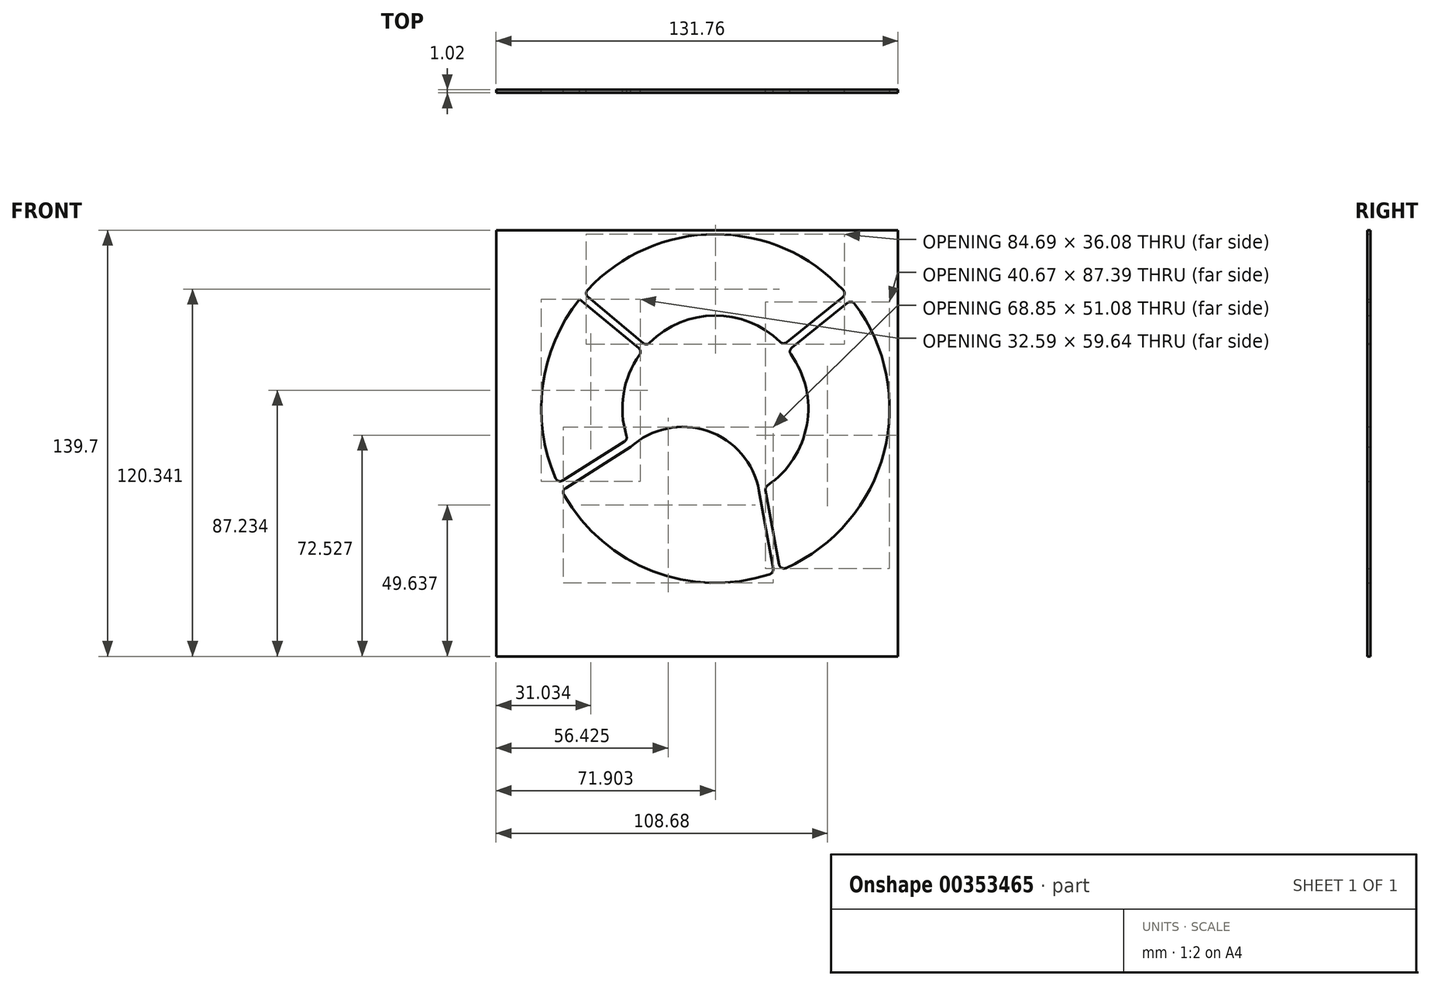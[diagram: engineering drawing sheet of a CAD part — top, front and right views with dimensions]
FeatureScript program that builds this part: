
annotation { "Feature Type Name" : "Feature", "Feature Type Description" : "" }
export const myFeature = defineFeature(function(context is Context, id is Id, definition is map)
    precondition{}
    {
        {
            var Q0;
            Q0=qCreatedBy(makeId("Front.planeOp"),FACE);
            var sketch = newSketch(context, id + "F0", { "sketchPlane" : qUnion([Q0])});
            skArc(sketch, "E0", {"start": v(-44.53, 35.83) * mm, "mid": v(-56.76, 6.66) * mm, "end": v(-51.6, -24.55) * mm});
            skArc(sketch, "E1", {"start": v(16.3, -25.76) * mm, "mid": v(30.05, -5.09) * mm, "end": v(23.86, 18.97) * mm});
            skLineSegment(sketch, "E2", {"start": v(22.25, 20.83) * mm, "end": v(43.08, 37.55) * mm});
            skLineSegment(sketch, "E3", {"start": v(23.86, 18.97) * mm, "end": v(44.66, 35.66) * mm});
            skLineSegment(sketch, "E4", {"start": v(-22.57, 20.48) * mm, "end": v(-43.03, 37.6) * mm});
            skLineSegment(sketch, "E5", {"start": v(-23.97, 18.83) * mm, "end": v(-44.53, 35.83) * mm});
            skArc(sketch, "E6", {"start": v(14.33, -26.9) * mm, "mid": v(-2.5, -7.36) * mm, "end": v(-27.75, -12.6) * mm});
            skLineSegment(sketch, "E7.bottom", {"start": v(-71.89, 58.47) * mm, "end": v(59.87, 58.47) * mm});
            skLineSegment(sketch, "E7.top", {"start": v(-71.89, -81.23) * mm, "end": v(59.87, -81.23) * mm});
            skLineSegment(sketch, "E7.left", {"start": v(-71.89, 58.47) * mm, "end": v(-71.89, -81.23) * mm});
            skLineSegment(sketch, "E7.right", {"start": v(59.87, 58.47) * mm, "end": v(59.87, -81.23) * mm});
            skLineSegment(sketch, "E8", {"start": v(14.33, -26.9) * mm, "end": v(19.18, -53.84) * mm});
            skLineSegment(sketch, "E9", {"start": v(-27.75, -12.6) * mm, "end": v(-50.42, -26.9) * mm});
            skLineSegment(sketch, "E10", {"start": v(-28.75, -10.14) * mm, "end": v(-51.6, -24.55) * mm});
            skLineSegment(sketch, "E11", {"start": v(16.3, -25.76) * mm, "end": v(21.26, -53.05) * mm});
            skArc(sketch, "E12.trimOffspring", {"start": v(-23.97, 18.83) * mm, "mid": v(-30.07, 4.96) * mm, "end": v(-28.75, -10.14) * mm});
            skArc(sketch, "E13.trimOffspring", {"start": v(22.25, 20.83) * mm, "mid": v(-0.24, 30.48) * mm, "end": v(-22.57, 20.48) * mm});
            skArc(sketch, "E14.trimOffspring", {"start": v(43.08, 37.55) * mm, "mid": v(0.04, 57.15) * mm, "end": v(-43.03, 37.6) * mm});
            skArc(sketch, "E15.trimOffspring", {"start": v(21.26, -53.05) * mm, "mid": v(55.26, -14.57) * mm, "end": v(44.66, 35.66) * mm});
            skArc(sketch, "E16.trimOffspring", {"start": v(-50.42, -26.9) * mm, "mid": v(-20.62, -53.3) * mm, "end": v(19.18, -53.84) * mm});
            skSolve(sketch);
        }
        {
            var Q0;
            Q0=makeQuery(id+"F0.imprint","IMPRINT",FACE,{"disambiguationData":[TD([[makeQuery(id+"F0.imprint","IMPRINT",EDGE,{"derivedFrom":sQuery(id+"F0.wireOp",EDGE,"E0")}),-1.0]])]});
            extrude(context, id + "F1", {"entities" : qUnion([Q0]), "depth" : 1.02 * mm});
        }
        {
            var Q0;
            Q0=makeQuery(id+"F1.opExtrude","SWEPT_EDGE",EDGE,{"disambiguationData":[OSD([sQuery(id+"F0.wireOp",EDGE,"E5"),sQuery(id+"F0.wireOp",EDGE,"E12.trimOffspring")])]});
            var Q1;
            Q1=makeQuery(id+"F1.opExtrude","SWEPT_EDGE",EDGE,{"disambiguationData":[OSD([sQuery(id+"F0.wireOp",EDGE,"E10"),sQuery(id+"F0.wireOp",EDGE,"E12.trimOffspring")])]});
            var Q2;
            Q2=makeQuery(id+"F1.opExtrude","SWEPT_EDGE",EDGE,{"disambiguationData":[OSD([sQuery(id+"F0.wireOp",EDGE,"E8"),sQuery(id+"F0.wireOp",EDGE,"E16.trimOffspring")])]});
            var Q3;
            Q3=makeQuery(id+"F1.opExtrude","SWEPT_EDGE",EDGE,{"disambiguationData":[OSD([sQuery(id+"F0.wireOp",EDGE,"E11"),sQuery(id+"F0.wireOp",EDGE,"E15.trimOffspring")])]});
            var Q4;
            Q4=makeQuery(id+"F1.opExtrude","SWEPT_EDGE",EDGE,{"disambiguationData":[OSD([sQuery(id+"F0.wireOp",EDGE,"E0"),sQuery(id+"F0.wireOp",EDGE,"E10")])]});
            var Q5;
            Q5=makeQuery(id+"F1.opExtrude","SWEPT_EDGE",EDGE,{"disambiguationData":[OSD([sQuery(id+"F0.wireOp",EDGE,"E2"),sQuery(id+"F0.wireOp",EDGE,"E13.trimOffspring")])]});
            var Q6;
            Q6=makeQuery(id+"F1.opExtrude","SWEPT_EDGE",EDGE,{"disambiguationData":[OSD([sQuery(id+"F0.wireOp",EDGE,"E4"),sQuery(id+"F0.wireOp",EDGE,"E13.trimOffspring")])]});
            var Q7;
            Q7=makeQuery(id+"F1.opExtrude","SWEPT_EDGE",EDGE,{"disambiguationData":[OSD([sQuery(id+"F0.wireOp",EDGE,"E1"),sQuery(id+"F0.wireOp",EDGE,"E3")])]});
            var Q8;
            Q8=makeQuery(id+"F1.opExtrude","SWEPT_EDGE",EDGE,{"disambiguationData":[OSD([sQuery(id+"F0.wireOp",EDGE,"E1"),sQuery(id+"F0.wireOp",EDGE,"E11")])]});
            var Q9;
            Q9=makeQuery(id+"F1.opExtrude","SWEPT_EDGE",EDGE,{"disambiguationData":[OSD([sQuery(id+"F0.wireOp",EDGE,"E4"),sQuery(id+"F0.wireOp",EDGE,"E14.trimOffspring")])]});
            var Q10;
            Q10=makeQuery(id+"F1.opExtrude","SWEPT_EDGE",EDGE,{"disambiguationData":[OSD([sQuery(id+"F0.wireOp",EDGE,"E9"),sQuery(id+"F0.wireOp",EDGE,"E16.trimOffspring")])]});
            var Q11;
            Q11=makeQuery(id+"F1.opExtrude","SWEPT_EDGE",EDGE,{"disambiguationData":[OSD([sQuery(id+"F0.wireOp",EDGE,"E2"),sQuery(id+"F0.wireOp",EDGE,"E14.trimOffspring")])]});
            var Q12;
            Q12=makeQuery(id+"F1.opExtrude","SWEPT_EDGE",EDGE,{"disambiguationData":[OSD([sQuery(id+"F0.wireOp",EDGE,"E3"),sQuery(id+"F0.wireOp",EDGE,"E15.trimOffspring")])]});
            fillet(context, id + "F2", {"entities" : qUnion([Q0, Q1, Q2, Q3, Q4, Q5, Q6, Q7, Q8, Q9, Q10, Q11, Q12]), "radius" : 1.6 * mm, "allowEdgeOverflow" : false});
        }
    });
